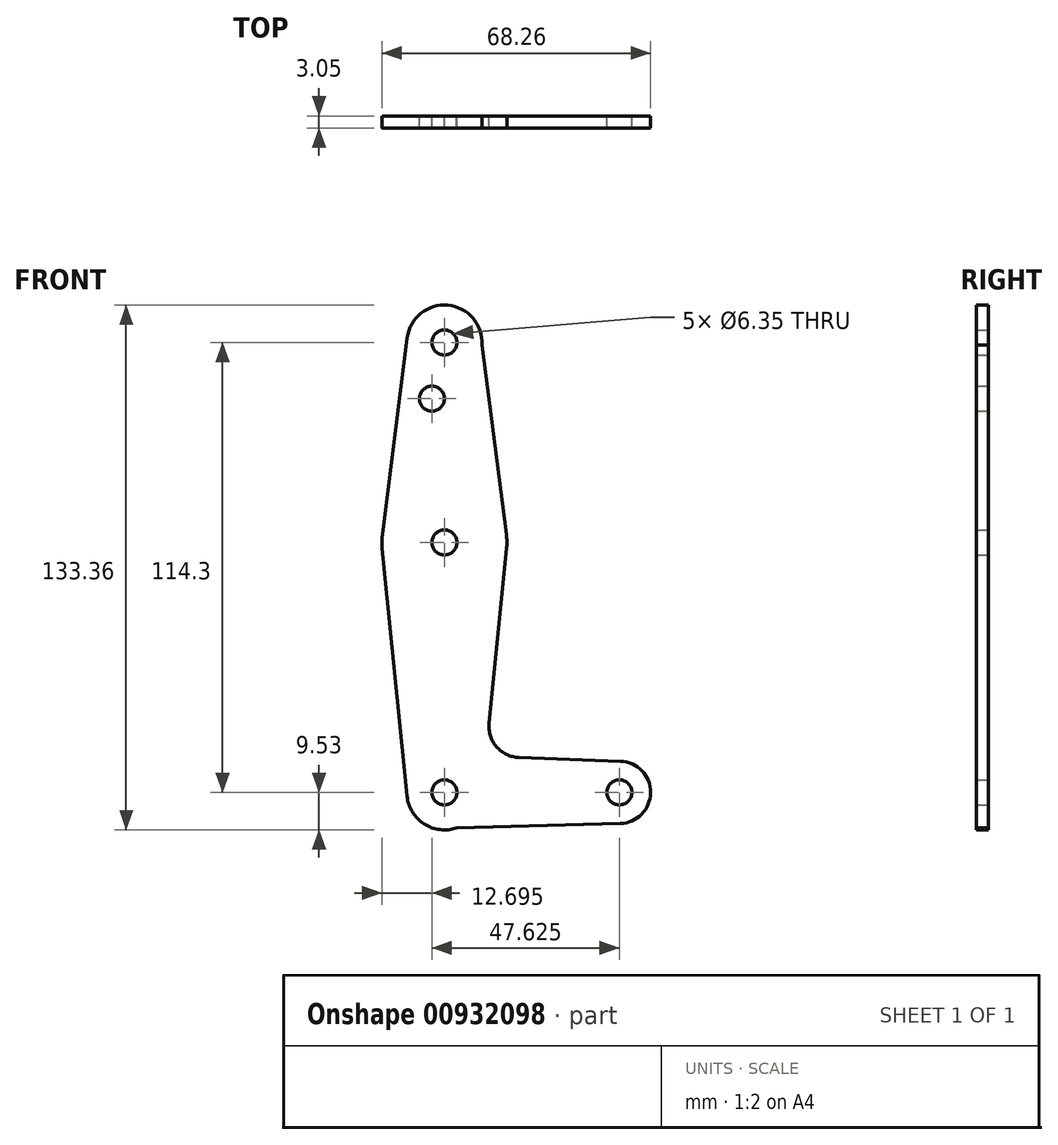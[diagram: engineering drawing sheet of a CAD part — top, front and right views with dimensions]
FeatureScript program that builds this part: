
annotation { "Feature Type Name" : "Feature", "Feature Type Description" : "" }
export const myFeature = defineFeature(function(context is Context, id is Id, definition is map)
    precondition{}
    {
        {
            var Q0;
            Q0=qCreatedBy(makeId("Front.planeOp"),FACE);
            var sketch = newSketch(context, id + "F0", { "sketchPlane" : qUnion([Q0])});
            skCircle(sketch, "E0", {"center": v(0, 0) * mm, "radius": 9.53 * mm});
            skLineSegment(sketch, "E1", {"start": v(0, 0) * mm, "end": v(0, 63.5) * mm});
            skCircle(sketch, "E2", {"center": v(0, 63.5) * mm, "radius": 15.88 * mm});
            skLineSegment(sketch, "E3", {"start": v(0, 63.5) * mm, "end": v(0, 114.3) * mm});
            skCircle(sketch, "E4", {"center": v(0, 114.3) * mm, "radius": 9.53 * mm});
            skLineSegment(sketch, "E5", {"start": v(0, 0) * mm, "end": v(44.45, 0) * mm});
            skCircle(sketch, "E6", {"center": v(44.45, 0) * mm, "radius": 7.94 * mm});
            skLineSegment(sketch, "E7", {"start": v(9.5, 113.7) * mm, "end": v(15.74, 65.54) * mm});
            skLineSegment(sketch, "E8", {"start": v(-9.45, 115.5) * mm, "end": v(-15.75, 65.48) * mm});
            skLineSegment(sketch, "E9", {"start": v(15.8, 61.91) * mm, "end": v(11.34, 17.6) * mm});
            skLineSegment(sketch, "E10", {"start": v(-15.8, 61.91) * mm, "end": v(-9.48, -0.95) * mm});
            skLineSegment(sketch, "E11", {"start": v(18.97, 8.85) * mm, "end": v(44.73, 7.93) * mm});
            skLineSegment(sketch, "E12", {"start": v(3.1, -9) * mm, "end": v(44.65, -7.93) * mm});
            skCircle(sketch, "E13", {"center": v(0, 114.3) * mm, "radius": 3.18 * mm});
            skCircle(sketch, "E14", {"center": v(-3.18, 100.03) * mm, "radius": 3.18 * mm});
            skPoint(sketch, "E15", {"position": v(0, 100.03) * mm});
            skCircle(sketch, "E16", {"center": v(0, 63.5) * mm, "radius": 3.18 * mm});
            skCircle(sketch, "E17", {"center": v(0, 0) * mm, "radius": 3.18 * mm});
            skCircle(sketch, "E18", {"center": v(44.45, 0) * mm, "radius": 3.18 * mm});
            skArc(sketch, "E19.filletArc", {"start": v(11.34, 17.6) * mm, "mid": v(13.26, 11.57) * mm, "end": v(18.97, 8.85) * mm});
            skSolve(sketch);
        }
        {
            var Q0;
            {var subQ0=sQuery(id+"F0.wireOp",EDGE,"E2");var subQ2=sQuery(id+"F0.wireOp",EDGE,"E1");var subQ3=makeQuery(id+"F0.imprint","INTERSECT",VERTEX,{"derivedFrom":[subQ2,subQ0]});Q0=makeQuery(id+"F0.imprint","IMPRINT",FACE,{"disambiguationData":[TD([[makeQuery(id+"F0.imprint","IMPRINT",EDGE,{"disambiguationData":[TD([[subQ3,-1.0]])],"derivedFrom":subQ2}),-1.0]])]});}
            var Q1;
            {var subQ0=sQuery(id+"F0.wireOp",EDGE,"E2");var subQ5=sQuery(id+"F0.wireOp",EDGE,"E1");var subQ6=makeQuery(id+"F0.imprint","INTERSECT",VERTEX,{"derivedFrom":[subQ5,subQ0]});Q1=makeQuery(id+"F0.imprint","IMPRINT",FACE,{"disambiguationData":[TD([[makeQuery(id+"F0.imprint","IMPRINT",EDGE,{"disambiguationData":[TD([[subQ6,-1.0]])],"derivedFrom":subQ5}),1.0]])]});}
            var Q2;
            {var subQ0=sQuery(id+"F0.wireOp",EDGE,"E8");Q2=makeQuery(id+"F0.imprint","IMPRINT",FACE,{"disambiguationData":[TD([[makeQuery(id+"F0.imprint","IMPRINT",EDGE,{"derivedFrom":subQ0}),1.0]])]});}
            var Q3;
            {var subQ0=sQuery(id+"F0.wireOp",EDGE,"E7");Q3=makeQuery(id+"F0.imprint","IMPRINT",FACE,{"disambiguationData":[TD([[makeQuery(id+"F0.imprint","IMPRINT",EDGE,{"derivedFrom":subQ0}),-1.0]])]});}
            var Q4;
            {var subQ5=sQuery(id+"F0.wireOp",EDGE,"E9");Q4=makeQuery(id+"F0.imprint","IMPRINT",FACE,{"disambiguationData":[TD([[makeQuery(id+"F0.imprint","IMPRINT",EDGE,{"derivedFrom":subQ5}),-1.0]])]});}
            var Q5;
            {var subQ0=sQuery(id+"F0.wireOp",EDGE,"E10");Q5=makeQuery(id+"F0.imprint","IMPRINT",FACE,{"disambiguationData":[TD([[makeQuery(id+"F0.imprint","IMPRINT",EDGE,{"derivedFrom":subQ0}),1.0]])]});}
            var Q6;
            {var subQ0=sQuery(id+"F0.wireOp",EDGE,"E1");var subQ1=sQuery(id+"F0.wireOp",EDGE,"E0");var subQ2=makeQuery(id+"F0.imprint","INTERSECT",VERTEX,{"derivedFrom":[subQ1,subQ0]});Q6=makeQuery(id+"F0.imprint","IMPRINT",FACE,{"disambiguationData":[TD([[makeQuery(id+"F0.imprint","IMPRINT",EDGE,{"disambiguationData":[TD([[subQ2,1.0]])],"derivedFrom":subQ1}),1.0]])]});}
            var Q7;
            {var subQ1=sQuery(id+"F0.wireOp",EDGE,"E0");var subQ8=makeQuery(id+"F0.imprint","INTERSECT",VERTEX,{"derivedFrom":[subQ1,sQuery(id+"F0.wireOp",EDGE,"E10")]});Q7=makeQuery(id+"F0.imprint","IMPRINT",FACE,{"disambiguationData":[TD([[makeQuery(id+"F0.imprint","IMPRINT",EDGE,{"disambiguationData":[TD([[subQ8,1.0]])],"derivedFrom":subQ1}),1.0]])]});}
            var Q8;
            Q8=makeQuery(id+"F0.imprint","IMPRINT",FACE,{"disambiguationData":[TD([[makeQuery(id+"F0.imprint","IMPRINT",EDGE,{"derivedFrom":sQuery(id+"F0.wireOp",EDGE,"E18")}),-1.0]])]});
            var Q9;
            {var subQ0=sQuery(id+"F0.wireOp",EDGE,"E12");Q9=makeQuery(id+"F0.imprint","IMPRINT",FACE,{"disambiguationData":[TD([[makeQuery(id+"F0.imprint","IMPRINT",EDGE,{"derivedFrom":subQ0}),1.0]])]});}
            var Q10;
            Q10=makeQuery(id+"F0.imprint","IMPRINT",FACE,{"disambiguationData":[TD([[makeQuery(id+"F0.imprint","IMPRINT",EDGE,{"derivedFrom":sQuery(id+"F0.wireOp",EDGE,"E13")}),-1.0]])]});
            extrude(context, id + "F1", {"entities" : qUnion([Q0, Q1, Q2, Q3, Q4, Q5, Q6, Q7, Q8, Q9, Q10]), "depth" : 3.05 * mm, "offsetDistance" : 25.4 * mm});
        }
    });
